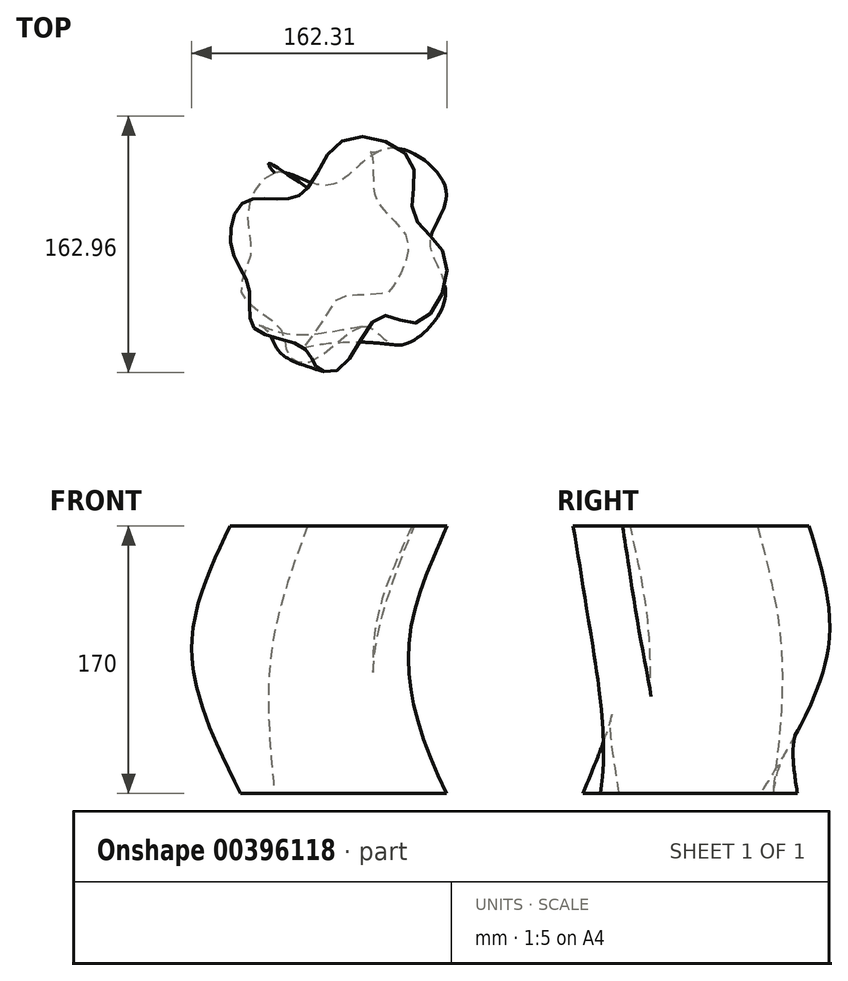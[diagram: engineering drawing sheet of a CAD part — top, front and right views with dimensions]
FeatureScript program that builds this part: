
annotation { "Feature Type Name" : "Feature", "Feature Type Description" : "" }
export const myFeature = defineFeature(function(context is Context, id is Id, definition is map)
    precondition{}
    {
        {
            var Q0;
            Q0=qCreatedBy(makeId("Top.planeOp"),FACE);
            var sketch = newSketch(context, id + "F0", { "sketchPlane" : qUnion([Q0])});
            skFitSpline(sketch, "E0", {"points": [v(-9.42, 47.07) * mm, v(-28.9, 46.54) * mm, v(-51.23, 52.2) * mm, v(-67.94, 27.95) * mm, v(-66.23, 0) * mm, v(-71.83, -24.72) * mm, v(-47.23, -46.58) * mm, v(-42.52, -62.73) * mm, v(-27.58, -67.33) * mm, v(6.34, -45.12) * mm, v(26.63, -57.09) * mm, v(57.55, -26.2) * mm, v(47.97, 8.58) * mm, v(58.11, 40.15) * mm, v(23.36, 68) * mm, v(-9.42, 47.07) * mm]});
            skSolve(sketch);
        }
        {
            var Q0;
            Q0=qCreatedBy(makeId("Top.planeOp"),FACE);
            cPlane(context, id + "F1", {"entities" : qUnion([Q0]), "cplaneType" : CPlaneType.OFFSET, "offset" : 93.98 * mm, "width" : 152.4 * mm, "height" : 152.4 * mm});
        }
        {
            var Q0;
            Q0=qCreatedBy(makeId("Top.planeOp"),FACE);
            cPlane(context, id + "F2", {"entities" : qUnion([Q0]), "cplaneType" : CPlaneType.OFFSET, "offset" : 170 * mm, "width" : 152.4 * mm, "height" : 152.4 * mm});
        }
        {
            var Q0;
            Q0=qCreatedBy(id+"F1.planeOp",FACE);
            var sketch = newSketch(context, id + "F3", { "sketchPlane" : qUnion([Q0])});
            skFitSpline(sketch, "E1", {"points": [v(-54.35, 55.01) * mm, v(-72.47, 47.85) * mm, v(-95.38, 45.52) * mm, v(-102.8, 17.03) * mm, v(-91.63, -8.65) * mm, v(-88.43, -33.8) * mm, v(-57.84, -45.93) * mm, v(-47.9, -59.49) * mm, v(-32.29, -58.7) * mm, v(-8, -26.23) * mm, v(15.16, -30.53) * mm, v(33.65, 9.06) * mm, v(12.75, 38.47) * mm, v(11.48, 71.6) * mm, v(-30.7, 85.88) * mm, v(-54.35, 55.01) * mm]});
            skSolve(sketch);
        }
        {
            var Q0;
            Q0=qCreatedBy(id+"F2.planeOp",FACE);
            var sketch = newSketch(context, id + "F4", { "sketchPlane" : qUnion([Q0])});
            skFitSpline(sketch, "E2", {"points": [v(-29.88, 42.67) * mm, v(-48, 35.5) * mm, v(-70.92, 33.18) * mm, v(-78.33, 4.69) * mm, v(-67.17, -21) * mm, v(-63.97, -46.14) * mm, v(-33.38, -58.27) * mm, v(-23.43, -71.83) * mm, v(-7.82, -71.04) * mm, v(16.46, -38.57) * mm, v(39.63, -42.87) * mm, v(58.12, -3.28) * mm, v(37.21, 26.13) * mm, v(35.95, 59.27) * mm, v(-6.23, 73.55) * mm, v(-29.88, 42.67) * mm]});
            skSolve(sketch);
        }
        {
            var Q0;
            Q0=makeQuery(id+"F4.imprint","IMPRINT",FACE,{"disambiguationData":[TD([[makeQuery(id+"F4.imprint","IMPRINT",EDGE,{"derivedFrom":sQuery(id+"F4.wireOp",EDGE,"E2")}),1.0]])]});
            var Q1;
            Q1=makeQuery(id+"F3.imprint","IMPRINT",FACE,{"disambiguationData":[TD([[makeQuery(id+"F3.imprint","IMPRINT",EDGE,{"derivedFrom":sQuery(id+"F3.wireOp",EDGE,"E1")}),1.0]])]});
            var Q2;
            Q2=makeQuery(id+"F0.imprint","IMPRINT",FACE,{"disambiguationData":[TD([[makeQuery(id+"F0.imprint","IMPRINT",EDGE,{"derivedFrom":sQuery(id+"F0.wireOp",EDGE,"E0")}),1.0]])]});
            loft(context, id + "F5", {"sheetProfilesArray" : [{ "sheetProfileEntities" : qUnion([Q0]) }, { "sheetProfileEntities" : qUnion([Q1]) }, { "sheetProfileEntities" : qUnion([Q2]) }]});
        }
    });
